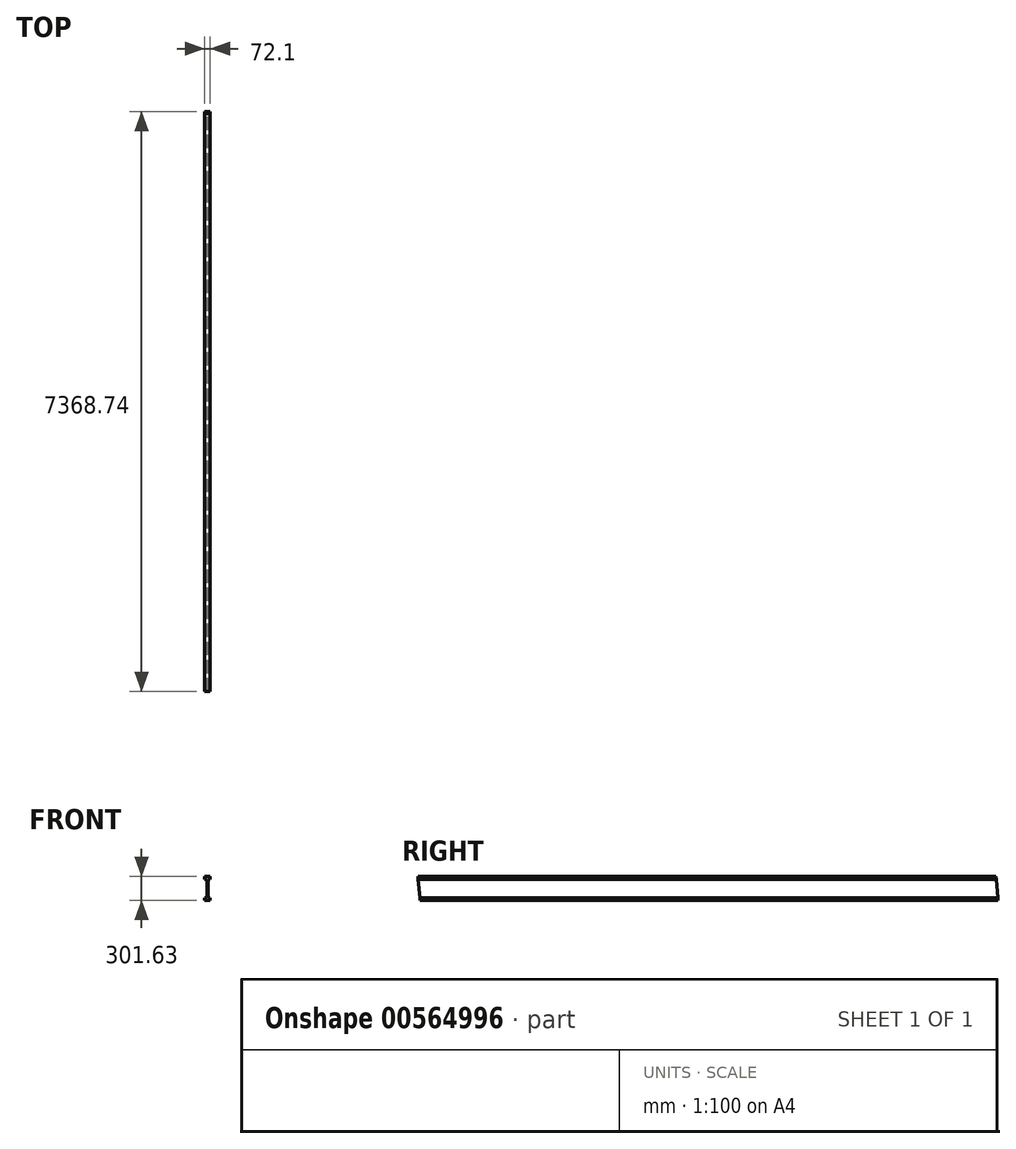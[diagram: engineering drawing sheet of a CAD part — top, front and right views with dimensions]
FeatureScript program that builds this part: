
annotation { "Feature Type Name" : "Feature", "Feature Type Description" : "" }
export const myFeature = defineFeature(function(context is Context, id is Id, definition is map)
    precondition{}
    {
        {
            var Q0;
            Q0=qCreatedBy(makeId("Front.planeOp"),FACE);
            var sketch = newSketch(context, id + "F0", { "sketchPlane" : qUnion([Q0])});
            skLineSegment(sketch, "E0", {"start": v(0, 0) * mm, "end": v(0, 33.65) * mm});
            skLineSegment(sketch, "E1", {"start": v(0, 33.65) * mm, "end": v(31.29, 33.65) * mm});
            skLineSegment(sketch, "E2", {"start": v(31.29, 33.65) * mm, "end": v(31.29, 267.97) * mm});
            skLineSegment(sketch, "E3", {"start": v(31.29, 267.97) * mm, "end": v(0, 267.97) * mm});
            skLineSegment(sketch, "E4", {"start": v(0, 267.97) * mm, "end": v(0, 301.63) * mm});
            skLineSegment(sketch, "E5", {"start": v(0, 301.63) * mm, "end": v(72.1, 301.63) * mm});
            skLineSegment(sketch, "E6", {"start": v(72.1, 301.63) * mm, "end": v(72.1, 267.97) * mm});
            skLineSegment(sketch, "E7", {"start": v(72.1, 267.97) * mm, "end": v(40.81, 267.97) * mm});
            skLineSegment(sketch, "E8", {"start": v(40.81, 267.97) * mm, "end": v(40.81, 33.65) * mm});
            skLineSegment(sketch, "E9", {"start": v(40.81, 33.65) * mm, "end": v(72.1, 33.66) * mm});
            skLineSegment(sketch, "E10", {"start": v(72.1, 33.66) * mm, "end": v(72.1, 0) * mm});
            skLineSegment(sketch, "E11", {"start": v(72.1, 0) * mm, "end": v(0, 0) * mm});
            skSolve(sketch);
        }
        {
            var Q0;
            Q0=qSketchRegion(id+"F0",true);
            extrude(context, id + "F1", {"entities" : qUnion([Q0]), "depth" : 7620 * mm});
        }
        {
            var Q0;
            Q0=makeQuery(id+"F1.opExtrude","SWEPT_FACE",FACE,{"disambiguationData":[OSD([sQuery(id+"F0.wireOp",EDGE,"E10")])]});
            var sketch = newSketch(context, id + "F2", { "sketchPlane" : qUnion([Q0])});
            skLineSegment(sketch, "E12", {"start": v(-140.22, 0) * mm, "end": v(-7149.76, -607.32) * mm, "construction": true});
            skLineSegment(sketch, "E13", {"start": v(-7149.76, -607.32) * mm, "end": v(-7202.38, 0) * mm, "construction": true});
            skLineSegment(sketch, "E14", {"start": v(-7202.38, 0) * mm, "end": v(-7342.6, 0) * mm, "construction": true});
            skLineSegment(sketch, "E15", {"start": v(-7342.6, 0) * mm, "end": v(-7368.74, 301.62) * mm});
            skLineSegment(sketch, "E16", {"start": v(-140.22, 0) * mm, "end": v(0, 0) * mm, "construction": true});
            skLineSegment(sketch, "E17", {"start": v(0, 0) * mm, "end": v(-26.13, 301.63) * mm});
            skLineSegment(sketch, "E18", {"start": v(-26.13, 301.63) * mm, "end": v(-7368.74, 301.62) * mm, "construction": true});
            skLineSegment(sketch, "E19", {"start": v(-7368.74, 301.62) * mm, "end": v(-7620, 301.62) * mm});
            skLineSegment(sketch, "E20", {"start": v(-7620, 301.63) * mm, "end": v(-7620, 0) * mm});
            skLineSegment(sketch, "E21", {"start": v(-7620, 0) * mm, "end": v(-7342.6, 0) * mm});
            skLineSegment(sketch, "E22", {"start": v(0, 0) * mm, "end": v(0, 301.63) * mm});
            skLineSegment(sketch, "E23", {"start": v(0, 301.63) * mm, "end": v(-26.13, 301.63) * mm});
            skSolve(sketch);
        }
        {
            var Q0;
            Q0=qSketchRegion(id+"F2",true);
            extrude(context, id + "F3", {"entities" : qUnion([Q0]), "operationType" : NewBodyOperationType.REMOVE, "endBound" : BoundingType.THROUGH_ALL, "oppositeDirection" : true, "depth" : 25.4 * mm, "offsetDistance" : 25.4 * mm});
        }
    });
